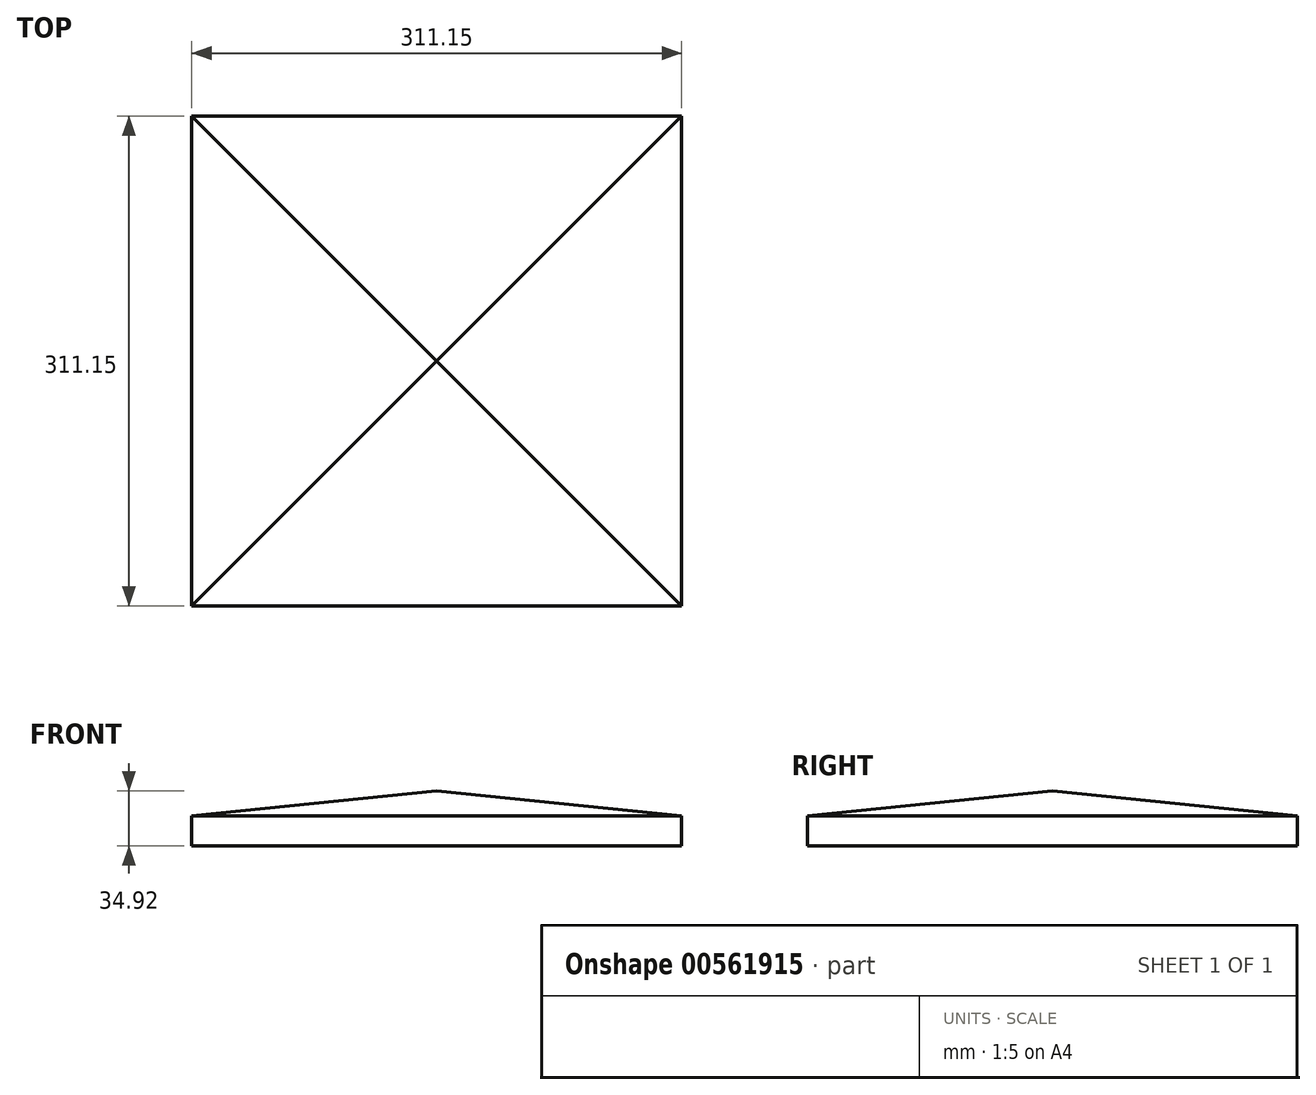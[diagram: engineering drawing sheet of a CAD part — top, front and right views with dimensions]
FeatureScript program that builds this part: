
annotation { "Feature Type Name" : "Feature", "Feature Type Description" : "" }
export const myFeature = defineFeature(function(context is Context, id is Id, definition is map)
    precondition{}
    {
        {
            var Q0;
            Q0=qCreatedBy(makeId("Front.planeOp"),FACE);
            var sketch = newSketch(context, id + "F0", { "sketchPlane" : qUnion([Q0])});
            skLineSegment(sketch, "E0.bottom", {"start": v(0, 0) * mm, "end": v(-311.15, 0) * mm});
            skLineSegment(sketch, "E0.left", {"start": v(0, 0) * mm, "end": v(0, 19.05) * mm});
            skLineSegment(sketch, "E0.right", {"start": v(-311.15, 0) * mm, "end": v(-311.15, 19.05) * mm});
            skLineSegment(sketch, "E1", {"start": v(-155.58, 34.93) * mm, "end": v(-155.58, 0) * mm, "construction": true});
            skLineSegment(sketch, "E2", {"start": v(-155.58, 34.93) * mm, "end": v(-311.15, 19.05) * mm});
            skLineSegment(sketch, "E3.MirrorCS", {"start": v(-155.58, 34.93) * mm, "end": v(0, 19.05) * mm});
            skPoint(sketch, "E4.orphan", {"position": v(-311.15, 34.93) * mm});
            skPoint(sketch, "E5.orphan", {"position": v(0, 34.93) * mm});
            skSolve(sketch);
        }
        {
            var Q0;
            Q0 = qSketchRegion(id + "F0", true);
            extrude(context, id + "F1", {"entities" : qUnion([Q0]), "oppositeDirection" : true, "depth" : 311.15 * mm, "offsetDistance" : 25.4 * mm});
        }
        {
            var Q0;
            Q0=makeQuery(id+"F1.opExtrude","SWEPT_FACE",FACE,{"disambiguationData":[OSD([sQuery(id+"F0.wireOp",EDGE,"E0.right")])]});
            var sketch = newSketch(context, id + "F2", { "sketchPlane" : qUnion([Q0])});
            skLineSegment(sketch, "E6.bottom", {"start": v(0, 0) * mm, "end": v(-311.15, 0) * mm});
            skLineSegment(sketch, "E6.left", {"start": v(0, 0) * mm, "end": v(0, 19.05) * mm});
            skLineSegment(sketch, "E6.right", {"start": v(-311.15, 0) * mm, "end": v(-311.15, 19.05) * mm});
            skLineSegment(sketch, "E7", {"start": v(-155.58, 34.93) * mm, "end": v(-155.58, 0) * mm, "construction": true});
            skLineSegment(sketch, "E8", {"start": v(-155.58, 34.93) * mm, "end": v(-311.15, 19.05) * mm});
            skLineSegment(sketch, "E9.MirrorCS", {"start": v(-155.58, 34.93) * mm, "end": v(0, 19.05) * mm});
            skPoint(sketch, "E10.orphan", {"position": v(-311.15, 34.93) * mm});
            skPoint(sketch, "E11.orphan", {"position": v(0, 34.93) * mm});
            skSolve(sketch);
        }
        {
            var Q0;
            Q0=makeQuery(id+"F2.imprint","IMPRINT",FACE,{"disambiguationData":[TD([[makeQuery(id+"F2.imprint","IMPRINT",EDGE,{"derivedFrom":sQuery(id+"F2.wireOp",EDGE,"E8")}),1.0]])]});
            var Q1;
            Q1=makeQuery(id+"F2.imprint","IMPRINT",FACE,{"disambiguationData":[TD([[makeQuery(id+"F2.imprint","IMPRINT",EDGE,{"derivedFrom":sQuery(id+"F2.wireOp",EDGE,"E6.bottom")}),1.0]])]});
            extrude(context, id + "F3", {"entities" : qUnion([Q0, Q1]), "operationType" : NewBodyOperationType.INTERSECT, "endBound" : BoundingType.THROUGH_ALL, "oppositeDirection" : true, "depth" : 25.4 * mm, "offsetDistance" : 25.4 * mm});
        }
    });
